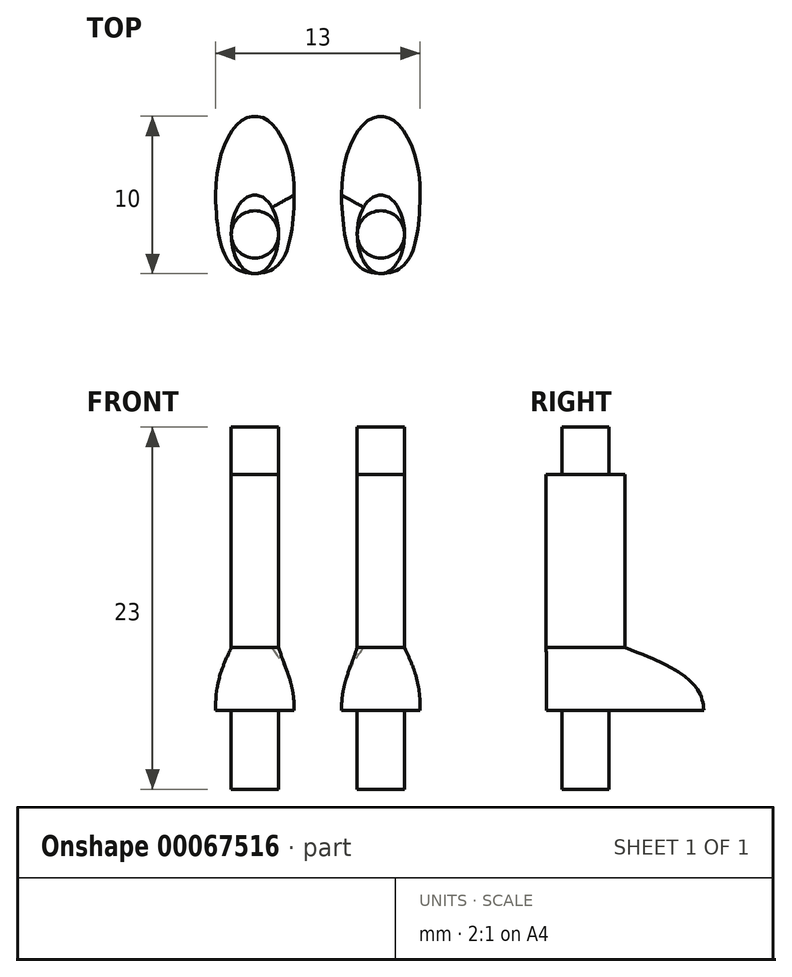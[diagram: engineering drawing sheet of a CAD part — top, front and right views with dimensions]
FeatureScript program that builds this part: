
annotation { "Feature Type Name" : "Feature", "Feature Type Description" : "" }
export const myFeature = defineFeature(function(context is Context, id is Id, definition is map)
    precondition{}
    {
        {
            var Q0;
            Q0=qCreatedBy(makeId("Top.planeOp"),FACE);
            var sketch = newSketch(context, id + "F0", { "sketchPlane" : qUnion([Q0])});
            skEllipticalArc(sketch, "E0", {});
            skPoint(sketch, "E1.endSnap0", {"position": v(-4, -10.09) * mm});
            skPoint(sketch, "E2.endSnap0", {"position": v(-1.5, -5.09) * mm});
            skFitSpline(sketch, "E3", {"points": [v(-6.5, -5.09) * mm, v(-4, -10.09) * mm], "startDerivative": vector(0.23, -9.72) * mm, "endDerivative": vector(5.86, 0) * mm});
            skLineSegment(sketch, "E4", {"start": v(-4, -5.09) * mm, "end": v(-4, -11.44) * mm, "construction": true});
            skFitSpline(sketch, "E5.MirrorCS", {"points": [v(-1.5, -5.09) * mm, v(-4, -10.09) * mm], "startDerivative": vector(-0.23, -9.72) * mm, "endDerivative": vector(-5.86, 0) * mm});
            const initialGuessF0  = {"E0": [-0.004, -0.005085160844027995, 0, 1, 0.005, 0.0025, 4.71238898038469, 1.5707963267948966]};
            skSetInitialGuess(sketch, initialGuessF0);
            skSolve(sketch);
        }
        {
            var Q0;
            Q0=qCreatedBy(makeId("Top.planeOp"),FACE);
            var sketch = newSketch(context, id + "F1", { "sketchPlane" : qUnion([Q0])});
            skEllipse(sketch, "E6", {"center": v(-4, -7.6) * mm, "majorRadius": 2.5 * mm, "minorRadius": 1.5 * mm, "majorAxis": v(0, -1)});
            skPoint(sketch, "E7.0", {"position": v(-4, -5.09) * mm});
            skSolve(sketch);
        }
        {
            var Q0;
            Q0=makeQuery(id+"F1.imprint","IMPRINT",FACE,{"disambiguationData":[TD([[makeQuery(id+"F1.imprint","IMPRINT",EDGE,{"derivedFrom":sQuery(id+"F1.wireOp",EDGE,"E6")}),1.0]])]});
            extrude(context, id + "F2", {"entities" : qUnion([Q0]), "depth" : 15 * mm, "hasSecondDirection" : true, "secondDirectionOppositeDirection" : false, "secondDirectionDepth" : 4 * mm});
        }
        {
            var Q1;
            Q1=makeQuery(id+"F0.imprint","IMPRINT",FACE,{"disambiguationData":[TD([[makeQuery(id+"F0.imprint","IMPRINT",EDGE,{"derivedFrom":sQuery(id+"F0.wireOp",EDGE,"E0")}),1.0]])]});
            var Q2;
            Q2=makeQuery(id+"F2.opExtrude","CAP_FACE",FACE,{"disambiguationData":[OSD([sQuery(id+"F1.wireOp",EDGE,"E6")])],"isStart":true});
            loft(context, id + "F3", {"operationType" : NewBodyOperationType.ADD, "startCondition" : LoftEndDerivativeType.NORMAL_TO_PROFILE, "startMagnitude" : 1.5, "sheetProfilesArray" : [{ "sheetProfileEntities" : qUnion([Q1]) }, { "sheetProfileEntities" : qUnion([Q2]) }]});
        }
        {
            var Q0;
            Q0=makeQuery(id+"F2.opExtrude","CAP_FACE",FACE,{"disambiguationData":[OSD([sQuery(id+"F1.wireOp",EDGE,"E6")])],"isStart":false});
            var sketch = newSketch(context, id + "F4", { "sketchPlane" : qUnion([Q0])});
            skCircle(sketch, "E8", {"center": v(-4, -7.6) * mm, "radius": 1.5 * mm});
            skSolve(sketch);
        }
        {
            var Q0;
            {var subQ0=sQuery(id+"F4.wireOp",EDGE,"E8");var subQ1=makeQuery(id+"F2.opExtrude","CAP_EDGE",EDGE,{"disambiguationData":[OSD([sQuery(id+"F1.wireOp",EDGE,"E6")])],"isStart":false});var subQ2=makeQuery(id+"F4.imprint","INTERSECT",VERTEX,{"disambiguationData":[OD(0.0)],"derivedFrom":[subQ1,subQ0]});Q0=makeQuery(id+"F4.imprint","IMPRINT",FACE,{"disambiguationData":[TD([[makeQuery(id+"F4.imprint","IMPRINT",EDGE,{"disambiguationData":[TD([[subQ2,1.0]])],"derivedFrom":subQ0}),1.0]])]});}
            extrude(context, id + "F5", {"entities" : qUnion([Q0]), "operationType" : NewBodyOperationType.ADD, "depth" : 3 * mm});
        }
        {
            var Q0;
            Q0=makeQuery(id+"F0.imprint","IMPRINT",FACE,{"disambiguationData":[TD([[makeQuery(id+"F0.imprint","IMPRINT",EDGE,{"derivedFrom":sQuery(id+"F0.wireOp",EDGE,"E0")}),1.0]])]});
            var sketch = newSketch(context, id + "F6", { "sketchPlane" : qUnion([Q0])});
            skCircle(sketch, "E9.0", {"center": v(-4, -7.6) * mm, "radius": 1.5 * mm});
            skSolve(sketch);
        }
        {
            var Q0;
            Q0=makeQuery(id+"F6.imprint","IMPRINT",FACE,{"disambiguationData":[TD([[makeQuery(id+"F6.imprint","IMPRINT",EDGE,{"derivedFrom":sQuery(id+"F6.wireOp",EDGE,"E9.0")}),1.0]])]});
            var Q1;
            Q1=sQuery(id+"F6.wireOp",EDGE,"E9.0");
            extrude(context, id + "F7", {"entities" : qUnion([Q0]), "operationType" : NewBodyOperationType.ADD, "surfaceEntities" : qUnion([Q1]), "oppositeDirection" : true, "depth" : 5 * mm});
        }
        {
            var Q0;
            Q0=makeQuery(id+"F2.opExtrude","SWEPT_BODY",BODY,{"disambiguationData":[OSD([sQuery(id+"F1.wireOp",EDGE,"E6")])]});
            var Q1;
            Q1=qCreatedBy(makeId("Right.planeOp"),FACE);
            mirror(context, id + "F8", {"entities" : qUnion([Q0]), "mirrorPlane" : qUnion([Q1])});
        }
    });
